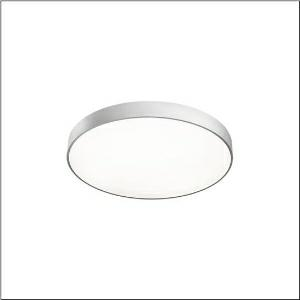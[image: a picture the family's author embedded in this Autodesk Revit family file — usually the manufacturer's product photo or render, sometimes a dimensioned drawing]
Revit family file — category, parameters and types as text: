
# Revit family: round_21_m_51mr36fd0421s
name_source: partatom
category: Lighting Fixtures
units: mm (PartAtom-declared; Revit-internal decimal feet)

## family parameters
Cut with Voids When Loaded = No
Host = Face
Light Source = No
Part Type = Normal
Room Calculation Point = No
Round Connector Dimension = Use Diameter
Shared = No

## types (1)
- Round 21 M (1 x LED, 7810 lm, 54.9 W, 4000K)
    Apparent Load = 55 VA
    CIE Flux Codes = 49 80 96 100 100
    Color Rendering = 80
    Color Temperature = 4000K
    Default Elevation = 1800 mm
    Description = Round 21 M, wall and ceiling luminaire, primary optical cover: cover, of PMMA, opal, light emission: direct distribution, primary light characteristic: symmetric, installation type: surface-mounted, suspended mounting, LED, rated luminous flux: 7.810lm, luminous efficacy: 142lm/W, light colour: 840, colour temperature: 4000K, control gear: DALI 2, with terminal, 5-pole, mains connection: 230V, AC, 50/60Hz, rated input power: 55W, housing, of aluminium, coated, silver, diameter: 600mm, height: 62mm, protection rating (complete): IP40, insulation class (complete): insulation class I (protective earthing), certification: CE, impact resistance: IK04, permissible operating ambient temperature: -10..+35°C, packaging unit: 1 piece
    Height = 87 mm
    Lamp = 1 x LED
    Lamp Light Flux = 7810 lm
    Lamp Power = 54.9 W
    Lamp count = 1
    Length = 600 mm
    Luminous efficacy = 142 lm/W
    Manufacturer = Siteco
    ModVariant = No
    Model = 51MR36FD0421S
    Mounting Place = Ceiling
    Mounting Type = Surface mounted
    Number of Poles = 1
    OnlyDefault = Yes
    Power Factor = 1
    Product Name = Round 21 M
    Product group = wall and ceiling luminaire | ceiling mounted
    ProductGroupID = 304
    Protection Class = Protection class I
    Protection Degree = IP 40
    RLX_Detail_Level = 1
    RLX_Emergency_Light_Flux = 0 lm
    RLX_Emergency_Type = 0
    RLX_Emergency_Type_DB = No
    RlxData = <blob elided: 14845 chars, md5=d2f1f778>
    Socket = socket
    Standby Power = 0 W
    System Light Flux = 7810 lm
    System Power = 55 W
    Type Comments = Product without accessories
    Type Image = l_1258303.jpg
    URL = http://relux.com
    VarID = ---
    Voltage = 0 V
    Weight = 0.00 kg
    Width = 0 mm  [stored 0 ft]

note: [stored X ft] marks values corroborated as IEEE doubles in the binary element streams (Revit-internal decimal feet)

## geometry (parser evidence)
native form markers: Sweep x9
no freeform markers — native parametric forms only
